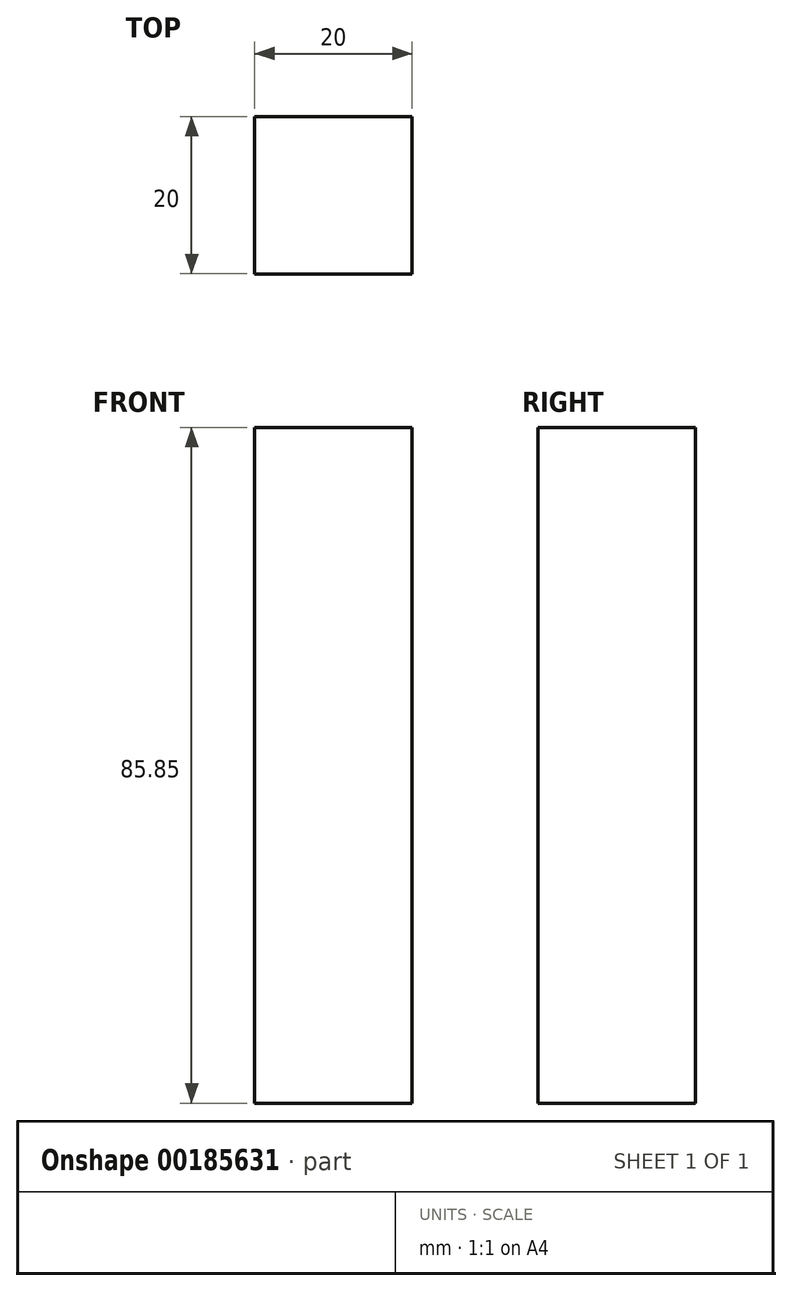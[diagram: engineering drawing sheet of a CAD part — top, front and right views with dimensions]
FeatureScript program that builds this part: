
annotation { "Feature Type Name" : "Feature", "Feature Type Description" : "" }
export const myFeature = defineFeature(function(context is Context, id is Id, definition is map)
    precondition{}
    {
        {
            var Q0;
            Q0=qCreatedBy(makeId("Top.planeOp"),FACE);
            var sketch = newSketch(context, id + "F0", { "sketchPlane" : qUnion([Q0])});
            skLineSegment(sketch, "E0.bottom", {"start": v(-2.14, 2.13) * mm, "end": v(17.86, 2.13) * mm});
            skLineSegment(sketch, "E0.top", {"start": v(-2.14, -17.87) * mm, "end": v(17.86, -17.87) * mm});
            skLineSegment(sketch, "E0.left", {"start": v(-2.14, 2.13) * mm, "end": v(-2.14, -17.87) * mm});
            skLineSegment(sketch, "E0.right", {"start": v(17.86, 2.13) * mm, "end": v(17.86, -17.87) * mm});
            skSolve(sketch);
        }
        {
            var Q0;
            Q0=makeQuery(id+"F0.imprint","IMPRINT",FACE,{"disambiguationData":[TD([[makeQuery(id+"F0.imprint","IMPRINT",EDGE,{"derivedFrom":sQuery(id+"F0.wireOp",EDGE,"E0.bottom")}),-1.0]])]});
            extrude(context, id + "F1", {"entities" : qUnion([Q0]), "depth" : 85.85 * mm});
        }
    });
